# Revit family: MOODY_LAMP RFL. SQUARE 100 FIX
name_source: partatom
category: Modelos genéricos
revit_build: Autodesk Revit 2015 (Build: 20140606_1530(x64)
units: mm (PartAtom-declared; Revit-internal decimal feet)

## types (4) — shared parameters
Accessory Type = Assembly
Dimensions = 100 x 100
Fabricante = LAMP
Last update = 29/08/2019
Manufacturer URL = http://www.lamp.es
Manufacturer country = Spain
Manufacturer name = LAMP
Material Muelle Emp. = LAMP_Acero genérico
Product URL = https://www.lamp.es
Product datasheet = https://www.lamp.es
Recessed dimensions = 95 x 95
Weight = 0.04 kg

## per-type parameters (varying)
| type | Descripción | Finish | Material Reflector | Modelo | Product code |
| WHITE FINISH | MOODY ACC. RFL. SQUARE 100 FIX WH. | Matt white | LAMP_PC Reflector Moody BL | MORFSQ100FXW | MORFSQ100FXW |
| COPPER FINISH | MOODY ACC. RFL. SQUARE 100 FIX CO. | Metalized matt copper | LAMP_PC Reflector Moody CO | MORFSQ100FXC | MORFSQ100FXC |
| BLACK FINISH | MOODY ACC. RFL. SQUARE 100 FIX BK. | Matt black | LAMP_PC Reflector Moody NG | MORFSQ100FXB | MORFSQ100FXB |
| SILVER FINISH | MOODY ACC. RFL. SQUARE 100 FIX MET. | Metalized matt silver | LAMP_PC Reflector Moody GR | MORFSQ100FXM | MORFSQ100FXM |
